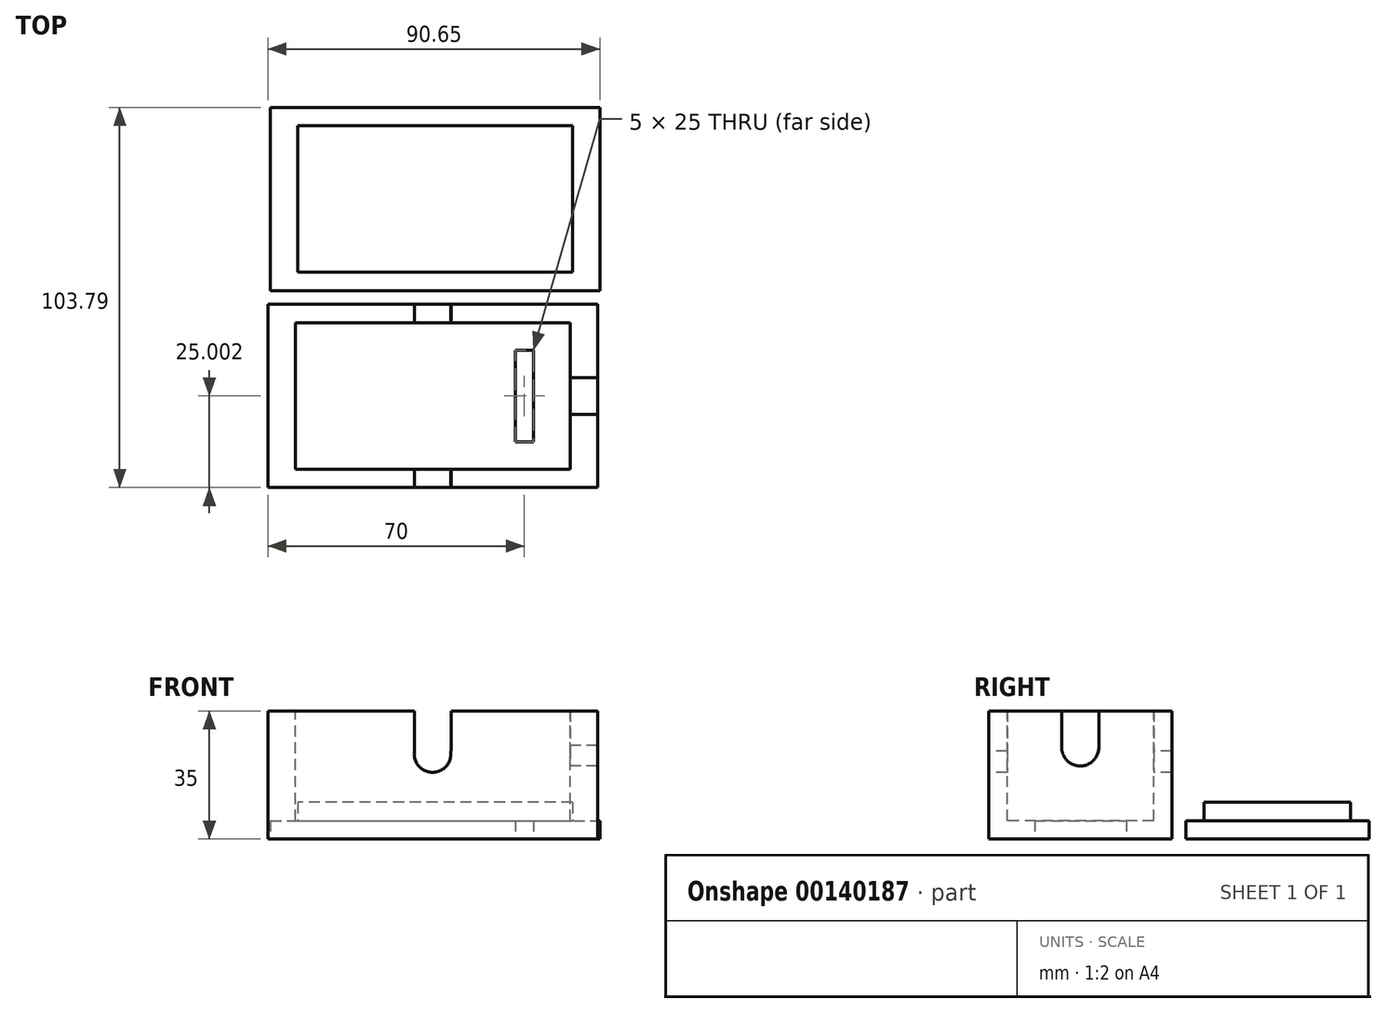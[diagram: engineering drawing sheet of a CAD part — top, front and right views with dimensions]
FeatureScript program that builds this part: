
annotation { "Feature Type Name" : "Feature", "Feature Type Description" : "" }
export const myFeature = defineFeature(function(context is Context, id is Id, definition is map)
    precondition{}
    {
        {
            var Q0;
            Q0=qCreatedBy(makeId("Top.planeOp"),FACE);
            var sketch = newSketch(context, id + "F0", { "sketchPlane" : qUnion([Q0])});
            skLineSegment(sketch, "E0.bottom", {"start": v(-40, 30.17) * mm, "end": v(50, 30.17) * mm});
            skLineSegment(sketch, "E0.top", {"start": v(-40, -19.83) * mm, "end": v(50, -19.83) * mm});
            skLineSegment(sketch, "E0.left", {"start": v(-40, 30.17) * mm, "end": v(-40, -19.83) * mm});
            skLineSegment(sketch, "E0.right", {"start": v(50, 30.17) * mm, "end": v(50, -19.83) * mm});
            skSolve(sketch);
        }
        {
            var Q0;
            Q0=makeQuery(id+"F0.imprint","IMPRINT",FACE,{"disambiguationData":[TD([[makeQuery(id+"F0.imprint","IMPRINT",EDGE,{"derivedFrom":sQuery(id+"F0.wireOp",EDGE,"E0.bottom")}),-1.0]])]});
            extrude(context, id + "F1", {"entities" : qUnion([Q0]), "depth" : 30 * mm});
        }
        {
            var Q0;
            Q0=makeQuery(id+"F1.opExtrude","CAP_FACE",FACE,{"disambiguationData":[OSD([sQuery(id+"F0.wireOp",EDGE,"E0.bottom"),sQuery(id+"F0.wireOp",EDGE,"E0.top"),sQuery(id+"F0.wireOp",EDGE,"E0.left"),sQuery(id+"F0.wireOp",EDGE,"E0.right")])],"isStart":false});
            var sketch = newSketch(context, id + "F2", { "sketchPlane" : qUnion([Q0])});
            skLineSegment(sketch, "E1.bottom", {"start": v(-32.5, 25.17) * mm, "end": v(42.5, 25.17) * mm});
            skLineSegment(sketch, "E1.top", {"start": v(-32.5, -14.83) * mm, "end": v(42.5, -14.83) * mm});
            skLineSegment(sketch, "E1.left", {"start": v(-32.5, 25.17) * mm, "end": v(-32.5, -14.83) * mm});
            skLineSegment(sketch, "E1.right", {"start": v(42.5, 25.17) * mm, "end": v(42.5, -14.83) * mm});
            skSolve(sketch);
        }
        {
            var Q0;
            Q0=makeQuery(id+"F2.imprint","IMPRINT",FACE,{"disambiguationData":[TD([[makeQuery(id+"F2.imprint","IMPRINT",EDGE,{"derivedFrom":sQuery(id+"F2.wireOp",EDGE,"E1.bottom")}),1.0]])]});
            var sketch = newSketch(context, id + "F3", { "sketchPlane" : qUnion([Q0])});
            skSolve(sketch);
        }
        {
            var Q0;
            Q0=makeQuery(id+"F2.imprint","IMPRINT",FACE,{"disambiguationData":[TD([[makeQuery(id+"F2.imprint","IMPRINT",EDGE,{"derivedFrom":sQuery(id+"F2.wireOp",EDGE,"E1.bottom")}),-1.0]])]});
            extrude(context, id + "F4", {"entities" : qUnion([Q0]), "operationType" : NewBodyOperationType.REMOVE, "oppositeDirection" : true, "depth" : 25 * mm});
        }
        {
            var Q0;
            Q0=makeQuery(id+"F1.opExtrude","CAP_FACE",FACE,{"disambiguationData":[OSD([sQuery(id+"F0.wireOp",EDGE,"E0.bottom"),sQuery(id+"F0.wireOp",EDGE,"E0.top"),sQuery(id+"F0.wireOp",EDGE,"E0.left"),sQuery(id+"F0.wireOp",EDGE,"E0.right")])],"isStart":true});
            var sketch = newSketch(context, id + "F5", { "sketchPlane" : qUnion([Q0])});
            skLineSegment(sketch, "E2.bottom", {"start": v(32.5, -17.67) * mm, "end": v(27.5, -17.67) * mm});
            skLineSegment(sketch, "E2.top", {"start": v(32.5, 7.33) * mm, "end": v(27.5, 7.33) * mm});
            skLineSegment(sketch, "E2.left", {"start": v(32.5, -17.67) * mm, "end": v(32.5, 7.33) * mm});
            skLineSegment(sketch, "E2.right", {"start": v(27.5, -17.67) * mm, "end": v(27.5, 7.33) * mm});
            skSolve(sketch);
        }
        {
            var Q0;
            Q0 = qSketchRegion(id + "F5", true);
            extrude(context, id + "F6", {"entities" : qUnion([Q0]), "operationType" : NewBodyOperationType.REMOVE, "oppositeDirection" : true, "depth" : 20 * mm});
        }
        {
            var Q0;
            Q0=makeQuery(id+"F3.imprint","IMPRINT",FACE,{"disambiguationData":[TD([[makeQuery(id+"F3.imprint","IMPRINT",EDGE,{"derivedFrom":makeQuery(id+"F2.imprint","IMPRINT",EDGE,{"derivedFrom":sQuery(id+"F2.wireOp",EDGE,"E1.bottom")})}),1.0]])]});
            extrude(context, id + "F7", {"entities" : qUnion([Q0]), "operationType" : NewBodyOperationType.ADD, "depth" : 5 * mm});
        }
        {
            var Q0;
            Q0=qCreatedBy(makeId("Top.planeOp"),FACE);
            var sketch = newSketch(context, id + "F8", { "sketchPlane" : qUnion([Q0])});
            skLineSegment(sketch, "E3.bottom", {"start": v(-39.35, 83.96) * mm, "end": v(50.65, 83.96) * mm});
            skLineSegment(sketch, "E3.top", {"start": v(-39.35, 33.96) * mm, "end": v(50.65, 33.96) * mm});
            skLineSegment(sketch, "E3.left", {"start": v(-39.35, 83.96) * mm, "end": v(-39.35, 33.96) * mm});
            skLineSegment(sketch, "E3.right", {"start": v(50.65, 83.96) * mm, "end": v(50.65, 33.96) * mm});
            skSolve(sketch);
        }
        {
            var Q0;
            Q0=makeQuery(id+"F8.imprint","IMPRINT",FACE,{"disambiguationData":[TD([[makeQuery(id+"F8.imprint","IMPRINT",EDGE,{"derivedFrom":sQuery(id+"F8.wireOp",EDGE,"E3.bottom")}),-1.0]])]});
            extrude(context, id + "F9", {"entities" : qUnion([Q0]), "depth" : 5 * mm});
        }
        {
            var Q0;
            Q0=qCreatedBy(makeId("Top.planeOp"),FACE);
            var sketch = newSketch(context, id + "F10", { "sketchPlane" : qUnion([Q0])});
            skLineSegment(sketch, "E4.bottom", {"start": v(43.15, 38.96) * mm, "end": v(-31.85, 38.96) * mm});
            skLineSegment(sketch, "E4.top", {"start": v(43.15, 78.97) * mm, "end": v(-31.85, 78.97) * mm});
            skLineSegment(sketch, "E4.left", {"start": v(43.15, 38.96) * mm, "end": v(43.15, 78.97) * mm});
            skLineSegment(sketch, "E4.right", {"start": v(-31.85, 38.96) * mm, "end": v(-31.85, 78.97) * mm});
            skSolve(sketch);
        }
        {
            var Q0;
            Q0=makeQuery(id+"F10.imprint","IMPRINT",FACE,{"disambiguationData":[TD([[makeQuery(id+"F10.imprint","IMPRINT",EDGE,{"derivedFrom":sQuery(id+"F10.wireOp",EDGE,"E4.bottom")}),-1.0]])]});
            extrude(context, id + "F11", {"entities" : qUnion([Q0]), "operationType" : NewBodyOperationType.ADD, "depth" : 10 * mm});
        }
        {
            var Q0;
            Q0=qCreatedBy(makeId("Front.planeOp"),FACE);
            var sketch = newSketch(context, id + "F12", { "sketchPlane" : qUnion([Q0])});
            skCircle(sketch, "E5", {"center": v(4.93, 23.19) * mm, "radius": 5 * mm});
            skLineSegment(sketch, "E6.bottom", {"start": v(10, 54) * mm, "end": v(0, 54) * mm});
            skLineSegment(sketch, "E6.top", {"start": v(10, 24) * mm, "end": v(0, 24) * mm});
            skLineSegment(sketch, "E6.left", {"start": v(10, 54) * mm, "end": v(10, 24) * mm});
            skLineSegment(sketch, "E6.right", {"start": v(0, 54) * mm, "end": v(0, 24) * mm});
            skSolve(sketch);
        }
        {
            var Q0;
            Q0 = qSketchRegion(id + "F12", true);
            extrude(context, id + "F13", {"entities" : qUnion([Q0]), "operationType" : NewBodyOperationType.REMOVE, "oppositeDirection" : true, "depth" : 53.36 * mm, "hasSecondDirection" : true, "secondDirectionOppositeDirection" : false, "secondDirectionDepth" : 52.64 * mm});
        }
        {
            var Q0;
            Q0=qCreatedBy(makeId("Right.planeOp"),FACE);
            var sketch = newSketch(context, id + "F14", { "sketchPlane" : qUnion([Q0])});
            skCircle(sketch, "E7", {"center": v(5.1, 25) * mm, "radius": 5.06 * mm});
            skLineSegment(sketch, "E8.bottom", {"start": v(0.08, 47.03) * mm, "end": v(10.17, 47.03) * mm});
            skLineSegment(sketch, "E8.top", {"start": v(0.08, 25) * mm, "end": v(10.17, 25) * mm});
            skLineSegment(sketch, "E8.left", {"start": v(0.08, 47.03) * mm, "end": v(0.08, 25) * mm});
            skLineSegment(sketch, "E8.right", {"start": v(10.17, 47.03) * mm, "end": v(10.17, 25) * mm});
            skSolve(sketch);
        }
        {
            var Q0;
            Q0 = qSketchRegion(id + "F14", true);
            extrude(context, id + "F15", {"entities" : qUnion([Q0]), "operationType" : NewBodyOperationType.REMOVE, "depth" : 79.26 * mm});
        }
    });
